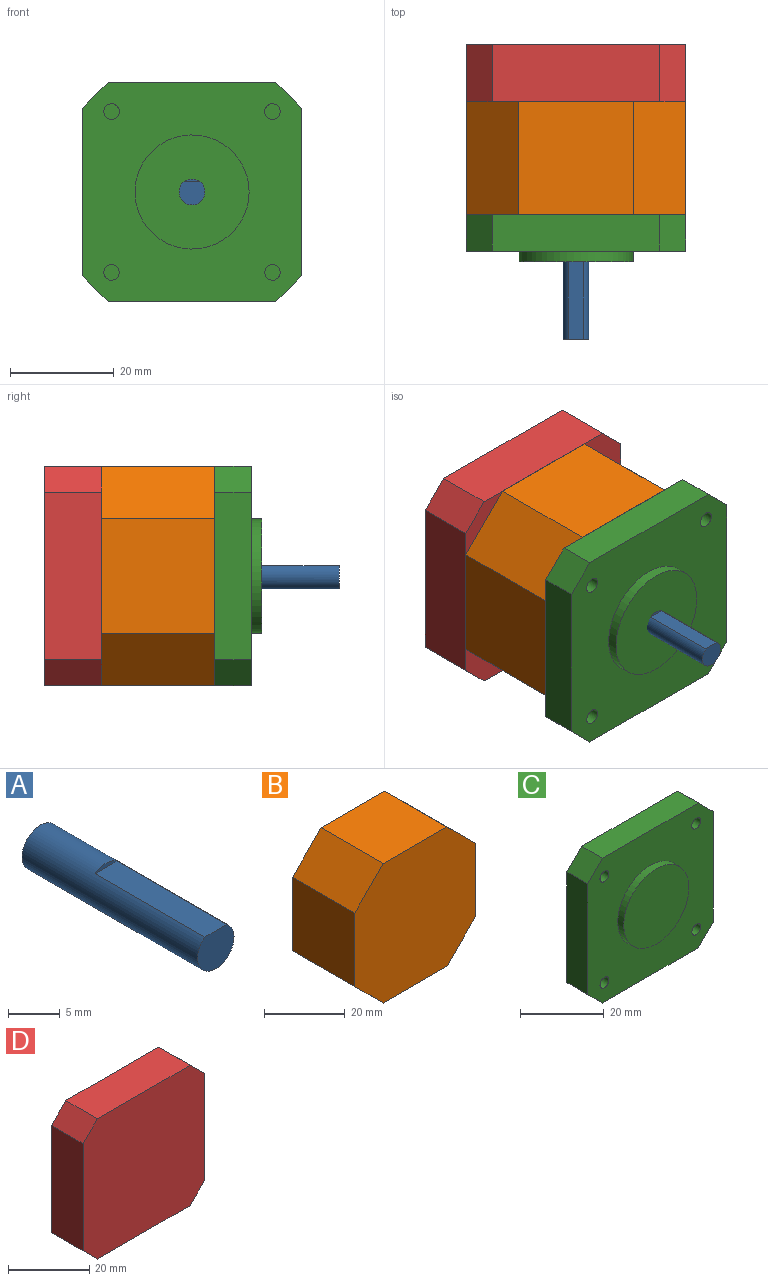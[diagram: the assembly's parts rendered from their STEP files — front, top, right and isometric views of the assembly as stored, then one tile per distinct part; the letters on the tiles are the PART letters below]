
ASSEMBLY  parts=4 mates=3
PART A: 5 faces, bbox 5x24x5 mm
  f0: cylinder r=2.5mm len=24mm, axis (0,1,0), area 328.7mm2, adj f1,f2,f3,f4
  f1: plane 5x4.5mm, normal (0,-1,0), area 18.6mm2, adj f0,f3
  f2: plane 5x5mm, normal (0,1,0), area 19.6mm2, adj f0
  f3: plane 15x3mm, normal (0,0,1), area 45mm2, adj f0,f1,f4
  f4: plane 3x0.5mm, normal (0,-1,0), area 1mm2, adj f0,f3
PART B: 10 faces, bbox 42.3x21.8x42.3 mm
  f0: plane 21.8x10mm, normal (0.71,0,0.71), area 308.3mm2, adj f3,f6,f7,f8
  f1: plane 21.8x10mm, normal (0.71,0,-0.71), area 308.3mm2, adj f3,f4,f6,f7
  f2: plane 21.8x10mm, normal (-0.71,0,0.71), area 308.3mm2, adj f6,f7,f8,f9
  f3: plane 22.3x21.8mm, normal (1,0,0), area 486.1mm2, adj f0,f1,f6,f7
  f4: plane 22.3x21.8mm, normal (0,0,-1), area 486.1mm2, adj f1,f5,f6,f7
  f5: plane 21.8x10mm, normal (-0.71,0,-0.71), area 308.3mm2, adj f4,f6,f7,f9
  f6: plane 42.3x42.3mm, normal (0,-1,0), area 1589.3mm2, adj f0,f1,f2,f3,f4,f5,f8,f9
  f7: plane 42.3x42.3mm, normal (0,1,0), area 1589.3mm2, adj f0,f1,f2,f3,f4,f5,f8,f9
  f8: plane 22.3x21.8mm, normal (0,0,1), area 486.1mm2, adj f0,f2,f6,f7
  f9: plane 22.3x21.8mm, normal (-1,0,0), area 486.1mm2, adj f2,f5,f6,f7
PART C: 20 faces, bbox 42.3x9x42.3 mm
  f0: plane 42.3x42.3mm, normal (0,-1,0), area 1330.9mm2, adj f1,f2,f3,f4,f6,f7,f8,f9
  f1: plane 32.3x7mm, normal (-1,0,0), area 226.1mm2, adj f0,f5,f6,f9
  f2: plane 32.3x7mm, normal (0,0,-1), area 226.1mm2, adj f0,f5,f6,f7
  f3: plane 32.3x7mm, normal (1,0,0), area 226.1mm2, adj f0,f5,f7,f8
  f4: plane 32.3x7mm, normal (0,0,1), area 226.1mm2, adj f0,f5,f8,f9
  f5: plane 42.3x42.3mm, normal (0,1,0), area 1739.3mm2, adj f1,f2,f3,f4,f6,f7,f8,f9
  f6: plane 7x5mm, normal (-0.71,0,-0.71), area 49.5mm2, adj f0,f1,f2,f5
  f7: plane 7x5mm, normal (0.71,0,-0.71), area 49.5mm2, adj f0,f2,f3,f5
  f8: plane 7x5mm, normal (0.71,0,0.71), area 49.5mm2, adj f0,f3,f4,f5
  f9: plane 7x5mm, normal (-0.71,0,0.71), area 49.5mm2, adj f0,f1,f4,f5
  f10: cylinder r=11mm len=22mm, axis (0,1,0), area 138.2mm2, adj f0,f11
  f11: plane 22x22mm, normal (0,-1,0), area 380.1mm2, adj f10
  f12: cylinder r=1.5mm len=4.5mm, axis (0,-1,0), area 42.4mm2, adj f0,f13
  f13: plane 3x3mm, normal (0,-1,0), area 7.1mm2, adj f12
  f14: cylinder r=1.5mm len=4.5mm, axis (0,-1,0), area 42.4mm2, adj f0,f15
  f15: plane 3x3mm, normal (0,-1,0), area 7.1mm2, adj f14
  f16: cylinder r=1.5mm len=4.5mm, axis (0,-1,0), area 42.4mm2, adj f0,f17
  f17: plane 3x3mm, normal (0,-1,0), area 7.1mm2, adj f16
  f18: cylinder r=1.5mm len=4.5mm, axis (0,-1,0), area 42.4mm2, adj f0,f19
  f19: plane 3x3mm, normal (0,-1,0), area 7.1mm2, adj f18
PART D: 18 faces, bbox 42.3x11x42.3 mm
  f0: plane 32.3x11mm, normal (1,0,0), area 355.3mm2, adj f4,f5,f8,f9
  f1: plane 32.3x11mm, normal (0,0,-1), area 355.3mm2, adj f4,f5,f7,f8
  f2: plane 32.3x11mm, normal (-1,0,0), area 355.3mm2, adj f4,f5,f6,f7
  f3: plane 32.3x11mm, normal (0,0,1), area 355.3mm2, adj f4,f5,f6,f9
  f4: plane 42.3x42.3mm, normal (0,1,0), area 1711mm2, adj f0,f1,f2,f3,f6,f7,f8,f9
  f5: plane 42.3x42.3mm, normal (0,-1,0), area 1739.3mm2, adj f0,f1,f2,f3,f6,f7,f8,f9
  f6: plane 11x5mm, normal (-0.71,0,0.71), area 77.8mm2, adj f2,f3,f4,f5
  f7: plane 11x5mm, normal (-0.71,0,-0.71), area 77.8mm2, adj f1,f2,f4,f5
  f8: plane 11x5mm, normal (0.71,0,-0.71), area 77.8mm2, adj f0,f1,f4,f5
  f9: plane 11x5mm, normal (0.71,0,0.71), area 77.8mm2, adj f0,f3,f4,f5
  f10: cylinder r=1.5mm len=4.5mm, axis (0,1,0), area 42.4mm2, adj f4,f11
  f11: plane 3x3mm, normal (0,1,0), area 7.1mm2, adj f10
  f12: cylinder r=1.5mm len=4.5mm, axis (0,1,0), area 42.4mm2, adj f4,f13
  f13: plane 3x3mm, normal (0,1,0), area 7.1mm2, adj f12
  f14: cylinder r=1.5mm len=4.5mm, axis (0,1,0), area 42.4mm2, adj f4,f15
  f15: plane 3x3mm, normal (0,1,0), area 7.1mm2, adj f14
  f16: cylinder r=1.5mm len=4.5mm, axis (0,1,0), area 42.4mm2, adj f4,f17
  f17: plane 3x3mm, normal (0,1,0), area 7.1mm2, adj f16
PLACE A t=(18.45,33,-13.43)mm
PLACE B t=(18.45,24,-13.43)mm
PLACE C t=(18.45,24,-13.43)mm
PLACE D t=(18.45,24,-13.43)mm
MATE fastened C.f10 <-> B.f6  axis (0,1,0) through (0,24,0)mm
MATE fastened A.f0 <-> B.f6  axis (0,1,0) through (0,24,0)mm
MATE fastened D.f5 <-> B.f7  axis (0,-1,0) through (0,45.8,0)mm
